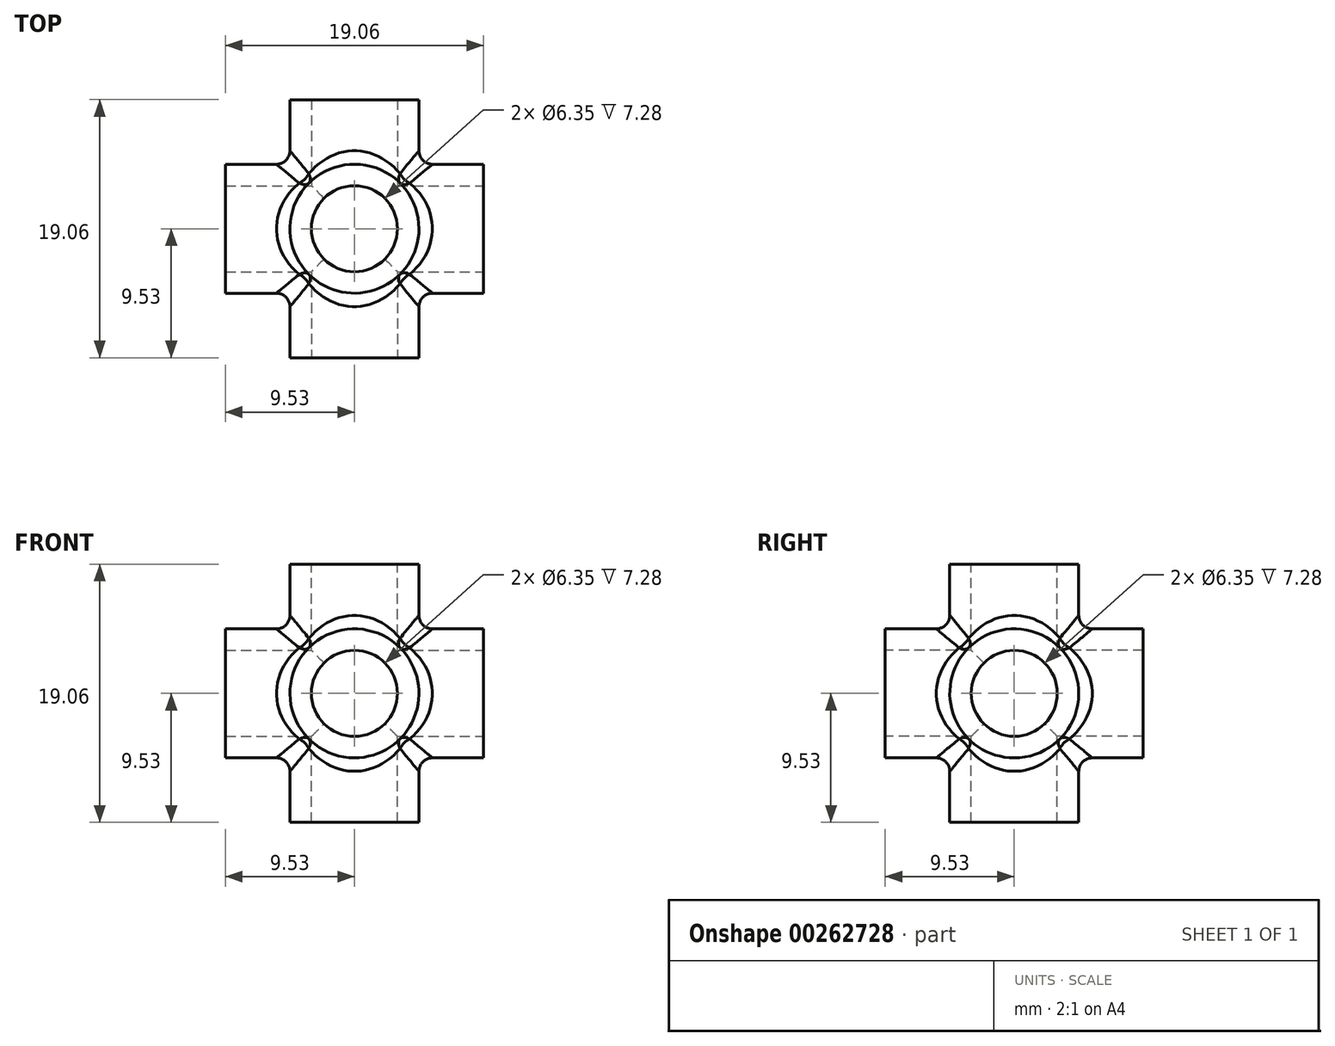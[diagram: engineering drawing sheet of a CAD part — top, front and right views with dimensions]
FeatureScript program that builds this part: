
annotation { "Feature Type Name" : "Feature", "Feature Type Description" : "" }
export const myFeature = defineFeature(function(context is Context, id is Id, definition is map)
    precondition{}
    {
        {
            var Q0;
            Q0=qCreatedBy(makeId("Front.planeOp"),FACE);
            var sketch = newSketch(context, id + "F0", { "sketchPlane" : qUnion([Q0])});
            skCircle(sketch, "E0", {"center": v(0, 0) * mm, "radius": 4.76 * mm});
            skSolve(sketch);
        }
        {
            var Q0;
            Q0 = qSketchRegion(id + "F0", true);
            extrude(context, id + "F1", {"entities" : qUnion([Q0]), "endBound" : BoundingType.SYMMETRIC, "depth" : 19.05 * mm});
        }
        {
            var Q0;
            Q0=qCreatedBy(makeId("Right.planeOp"),FACE);
            var sketch = newSketch(context, id + "F2", { "sketchPlane" : qUnion([Q0])});
            skCircle(sketch, "E1", {"center": v(0, 0) * mm, "radius": 4.76 * mm});
            skSolve(sketch);
        }
        {
            var Q0;
            Q0 = qSketchRegion(id + "F2", true);
            extrude(context, id + "F3", {"entities" : qUnion([Q0]), "operationType" : NewBodyOperationType.ADD, "endBound" : BoundingType.SYMMETRIC, "depth" : 19.05 * mm});
        }
        {
            var Q0;
            Q0=qCreatedBy(makeId("Top.planeOp"),FACE);
            var sketch = newSketch(context, id + "F4", { "sketchPlane" : qUnion([Q0])});
            skCircle(sketch, "E2", {"center": v(0, 0) * mm, "radius": 4.76 * mm});
            skSolve(sketch);
        }
        {
            var Q0;
            Q0 = qSketchRegion(id + "F4", true);
            extrude(context, id + "F5", {"entities" : qUnion([Q0]), "operationType" : NewBodyOperationType.ADD, "endBound" : BoundingType.SYMMETRIC, "depth" : 19.05 * mm});
        }
        {
            var Q0;
            Q0=makeQuery(id+"F1.opExtrude","CAP_FACE",FACE,{"disambiguationData":[OSD([sQuery(id+"F0.wireOp",EDGE,"E0")])],"isStart":false});
            var sketch = newSketch(context, id + "F6", { "sketchPlane" : qUnion([Q0])});
            skCircle(sketch, "E3", {"center": v(0, 0) * mm, "radius": 3.18 * mm});
            skSolve(sketch);
        }
        {
            var Q0;
            Q0 = qSketchRegion(id + "F6", true);
            extrude(context, id + "F7", {"entities" : qUnion([Q0]), "operationType" : NewBodyOperationType.REMOVE, "oppositeDirection" : true, "depth" : 20 * mm});
        }
        {
            var Q0;
            Q0=makeQuery(id+"F3.opExtrude","CAP_FACE",FACE,{"disambiguationData":[OSD([sQuery(id+"F2.wireOp",EDGE,"E1")])],"isStart":false});
            var sketch = newSketch(context, id + "F8", { "sketchPlane" : qUnion([Q0])});
            skCircle(sketch, "E4", {"center": v(0, 0) * mm, "radius": 3.18 * mm});
            skSolve(sketch);
        }
        {
            var Q0;
            Q0=makeQuery(id+"F8.imprint","IMPRINT",FACE,{"disambiguationData":[TD([[makeQuery(id+"F8.imprint","IMPRINT",EDGE,{"derivedFrom":sQuery(id+"F8.wireOp",EDGE,"E4")}),1.0]])]});
            extrude(context, id + "F9", {"entities" : qUnion([Q0]), "operationType" : NewBodyOperationType.REMOVE, "oppositeDirection" : true, "depth" : 20 * mm});
        }
        {
            var Q0;
            Q0=makeQuery(id+"F5.opExtrude","CAP_FACE",FACE,{"disambiguationData":[OSD([sQuery(id+"F4.wireOp",EDGE,"E2")])],"isStart":false});
            var sketch = newSketch(context, id + "F10", { "sketchPlane" : qUnion([Q0])});
            skCircle(sketch, "E5", {"center": v(0, 0) * mm, "radius": 3.18 * mm});
            skSolve(sketch);
        }
        {
            var Q0;
            Q0=makeQuery(id+"F10.imprint","IMPRINT",FACE,{"disambiguationData":[TD([[makeQuery(id+"F10.imprint","IMPRINT",EDGE,{"derivedFrom":sQuery(id+"F10.wireOp",EDGE,"E5")}),1.0]])]});
            extrude(context, id + "F11", {"entities" : qUnion([Q0]), "operationType" : NewBodyOperationType.REMOVE, "oppositeDirection" : true, "depth" : 20 * mm});
        }
        {
            var Q0;
            {var subQ0=sQuery(id+"F2.wireOp",EDGE,"E1");var subQ1=makeQuery(id+"F3.opExtrude","SWEPT_FACE",FACE,{"disambiguationData":[OSD([subQ0])]});Q0=makeQuery(id+"F5.boolean.opBoolean","INTERSECT",EDGE,{"disambiguationData":[OD(1.0)],"derivedFrom":[makeQuery(id+"F3.boolean.opBoolean","SPLIT",FACE,{"disambiguationData":[TD([makeQuery(id+"F3.opExtrude","CAP_FACE",FACE,{"disambiguationData":[OSD([subQ0])],"isStart":true})])],"derivedFrom":subQ1}),makeQuery(id+"F5.opExtrude","SWEPT_FACE",FACE,{"disambiguationData":[OSD([sQuery(id+"F4.wireOp",EDGE,"E2")])]})]});}
            var Q1;
            {var subQ0=sQuery(id+"F0.wireOp",EDGE,"E0");var subQ1=makeQuery(id+"F1.opExtrude","SWEPT_FACE",FACE,{"disambiguationData":[OSD([subQ0])]});Q1=makeQuery(id+"F5.boolean.opBoolean","INTERSECT",EDGE,{"disambiguationData":[OD(1.0)],"derivedFrom":[makeQuery(id+"F3.boolean.opBoolean","SPLIT",FACE,{"disambiguationData":[TD([makeQuery(id+"F1.opExtrude","CAP_FACE",FACE,{"disambiguationData":[OSD([subQ0])],"isStart":false})])],"derivedFrom":subQ1}),makeQuery(id+"F5.opExtrude","SWEPT_FACE",FACE,{"disambiguationData":[OSD([sQuery(id+"F4.wireOp",EDGE,"E2")])]})]});}
            var Q2;
            Q2=makeQuery(id+"F3.boolean.opBoolean","INTERSECT",EDGE,{"disambiguationData":[OD(2.0)],"derivedFrom":[makeQuery(id+"F1.opExtrude","SWEPT_FACE",FACE,{"disambiguationData":[OSD([sQuery(id+"F0.wireOp",EDGE,"E0")])]}),makeQuery(id+"F3.opExtrude","SWEPT_FACE",FACE,{"disambiguationData":[OSD([sQuery(id+"F2.wireOp",EDGE,"E1")])]})]});
            var Q3;
            {var subQ0=sQuery(id+"F2.wireOp",EDGE,"E1");var subQ1=makeQuery(id+"F3.opExtrude","SWEPT_FACE",FACE,{"disambiguationData":[OSD([subQ0])]});Q3=makeQuery(id+"F5.boolean.opBoolean","INTERSECT",EDGE,{"disambiguationData":[OD(0.0)],"derivedFrom":[makeQuery(id+"F3.boolean.opBoolean","SPLIT",FACE,{"disambiguationData":[TD([makeQuery(id+"F3.opExtrude","CAP_FACE",FACE,{"disambiguationData":[OSD([subQ0])],"isStart":true})])],"derivedFrom":subQ1}),makeQuery(id+"F5.opExtrude","SWEPT_FACE",FACE,{"disambiguationData":[OSD([sQuery(id+"F4.wireOp",EDGE,"E2")])]})]});}
            var Q4;
            {var subQ0=sQuery(id+"F0.wireOp",EDGE,"E0");var subQ1=makeQuery(id+"F1.opExtrude","SWEPT_FACE",FACE,{"disambiguationData":[OSD([subQ0])]});Q4=makeQuery(id+"F5.boolean.opBoolean","INTERSECT",EDGE,{"disambiguationData":[OD(0.0)],"derivedFrom":[makeQuery(id+"F3.boolean.opBoolean","SPLIT",FACE,{"disambiguationData":[TD([makeQuery(id+"F1.opExtrude","CAP_FACE",FACE,{"disambiguationData":[OSD([subQ0])],"isStart":false})])],"derivedFrom":subQ1}),makeQuery(id+"F5.opExtrude","SWEPT_FACE",FACE,{"disambiguationData":[OSD([sQuery(id+"F4.wireOp",EDGE,"E2")])]})]});}
            var Q5;
            Q5=makeQuery(id+"F3.boolean.opBoolean","INTERSECT",EDGE,{"disambiguationData":[OD(3.0)],"derivedFrom":[makeQuery(id+"F1.opExtrude","SWEPT_FACE",FACE,{"disambiguationData":[OSD([sQuery(id+"F0.wireOp",EDGE,"E0")])]}),makeQuery(id+"F3.opExtrude","SWEPT_FACE",FACE,{"disambiguationData":[OSD([sQuery(id+"F2.wireOp",EDGE,"E1")])]})]});
            var Q6;
            {var subQ0=sQuery(id+"F2.wireOp",EDGE,"E1");var subQ1=makeQuery(id+"F3.opExtrude","SWEPT_FACE",FACE,{"disambiguationData":[OSD([subQ0])]});Q6=makeQuery(id+"F5.boolean.opBoolean","INTERSECT",EDGE,{"disambiguationData":[OD(1.0)],"derivedFrom":[makeQuery(id+"F3.boolean.opBoolean","SPLIT",FACE,{"disambiguationData":[TD([makeQuery(id+"F3.opExtrude","CAP_FACE",FACE,{"disambiguationData":[OSD([subQ0])],"isStart":false})])],"derivedFrom":subQ1}),makeQuery(id+"F5.opExtrude","SWEPT_FACE",FACE,{"disambiguationData":[OSD([sQuery(id+"F4.wireOp",EDGE,"E2")])]})]});}
            var Q7;
            {var subQ0=sQuery(id+"F2.wireOp",EDGE,"E1");var subQ1=makeQuery(id+"F3.opExtrude","SWEPT_FACE",FACE,{"disambiguationData":[OSD([subQ0])]});Q7=makeQuery(id+"F5.boolean.opBoolean","INTERSECT",EDGE,{"disambiguationData":[OD(0.0)],"derivedFrom":[makeQuery(id+"F3.boolean.opBoolean","SPLIT",FACE,{"disambiguationData":[TD([makeQuery(id+"F3.opExtrude","CAP_FACE",FACE,{"disambiguationData":[OSD([subQ0])],"isStart":false})])],"derivedFrom":subQ1}),makeQuery(id+"F5.opExtrude","SWEPT_FACE",FACE,{"disambiguationData":[OSD([sQuery(id+"F4.wireOp",EDGE,"E2")])]})]});}
            var Q8;
            Q8=makeQuery(id+"F3.boolean.opBoolean","INTERSECT",EDGE,{"disambiguationData":[OD(1.0)],"derivedFrom":[makeQuery(id+"F1.opExtrude","SWEPT_FACE",FACE,{"disambiguationData":[OSD([sQuery(id+"F0.wireOp",EDGE,"E0")])]}),makeQuery(id+"F3.opExtrude","SWEPT_FACE",FACE,{"disambiguationData":[OSD([sQuery(id+"F2.wireOp",EDGE,"E1")])]})]});
            var Q9;
            {var subQ0=sQuery(id+"F0.wireOp",EDGE,"E0");var subQ1=makeQuery(id+"F1.opExtrude","SWEPT_FACE",FACE,{"disambiguationData":[OSD([subQ0])]});Q9=makeQuery(id+"F5.boolean.opBoolean","INTERSECT",EDGE,{"disambiguationData":[OD(1.0)],"derivedFrom":[makeQuery(id+"F3.boolean.opBoolean","SPLIT",FACE,{"disambiguationData":[TD([makeQuery(id+"F1.opExtrude","CAP_FACE",FACE,{"disambiguationData":[OSD([subQ0])],"isStart":true})])],"derivedFrom":subQ1}),makeQuery(id+"F5.opExtrude","SWEPT_FACE",FACE,{"disambiguationData":[OSD([sQuery(id+"F4.wireOp",EDGE,"E2")])]})]});}
            var Q10;
            Q10=makeQuery(id+"F3.boolean.opBoolean","INTERSECT",EDGE,{"disambiguationData":[OD(0.0)],"derivedFrom":[makeQuery(id+"F1.opExtrude","SWEPT_FACE",FACE,{"disambiguationData":[OSD([sQuery(id+"F0.wireOp",EDGE,"E0")])]}),makeQuery(id+"F3.opExtrude","SWEPT_FACE",FACE,{"disambiguationData":[OSD([sQuery(id+"F2.wireOp",EDGE,"E1")])]})]});
            var Q11;
            {var subQ0=sQuery(id+"F0.wireOp",EDGE,"E0");var subQ1=makeQuery(id+"F1.opExtrude","SWEPT_FACE",FACE,{"disambiguationData":[OSD([subQ0])]});Q11=makeQuery(id+"F5.boolean.opBoolean","INTERSECT",EDGE,{"disambiguationData":[OD(0.0)],"derivedFrom":[makeQuery(id+"F3.boolean.opBoolean","SPLIT",FACE,{"disambiguationData":[TD([makeQuery(id+"F1.opExtrude","CAP_FACE",FACE,{"disambiguationData":[OSD([subQ0])],"isStart":true})])],"derivedFrom":subQ1}),makeQuery(id+"F5.opExtrude","SWEPT_FACE",FACE,{"disambiguationData":[OSD([sQuery(id+"F4.wireOp",EDGE,"E2")])]})]});}
            fillet(context, id + "F12", {"entities" : qUnion([Q0, Q1, Q2, Q3, Q4, Q5, Q6, Q7, Q8, Q9, Q10, Q11]), "radius" : 1 * mm, "tangentPropagation" : true, "allowEdgeOverflow" : false});
        }
    });
